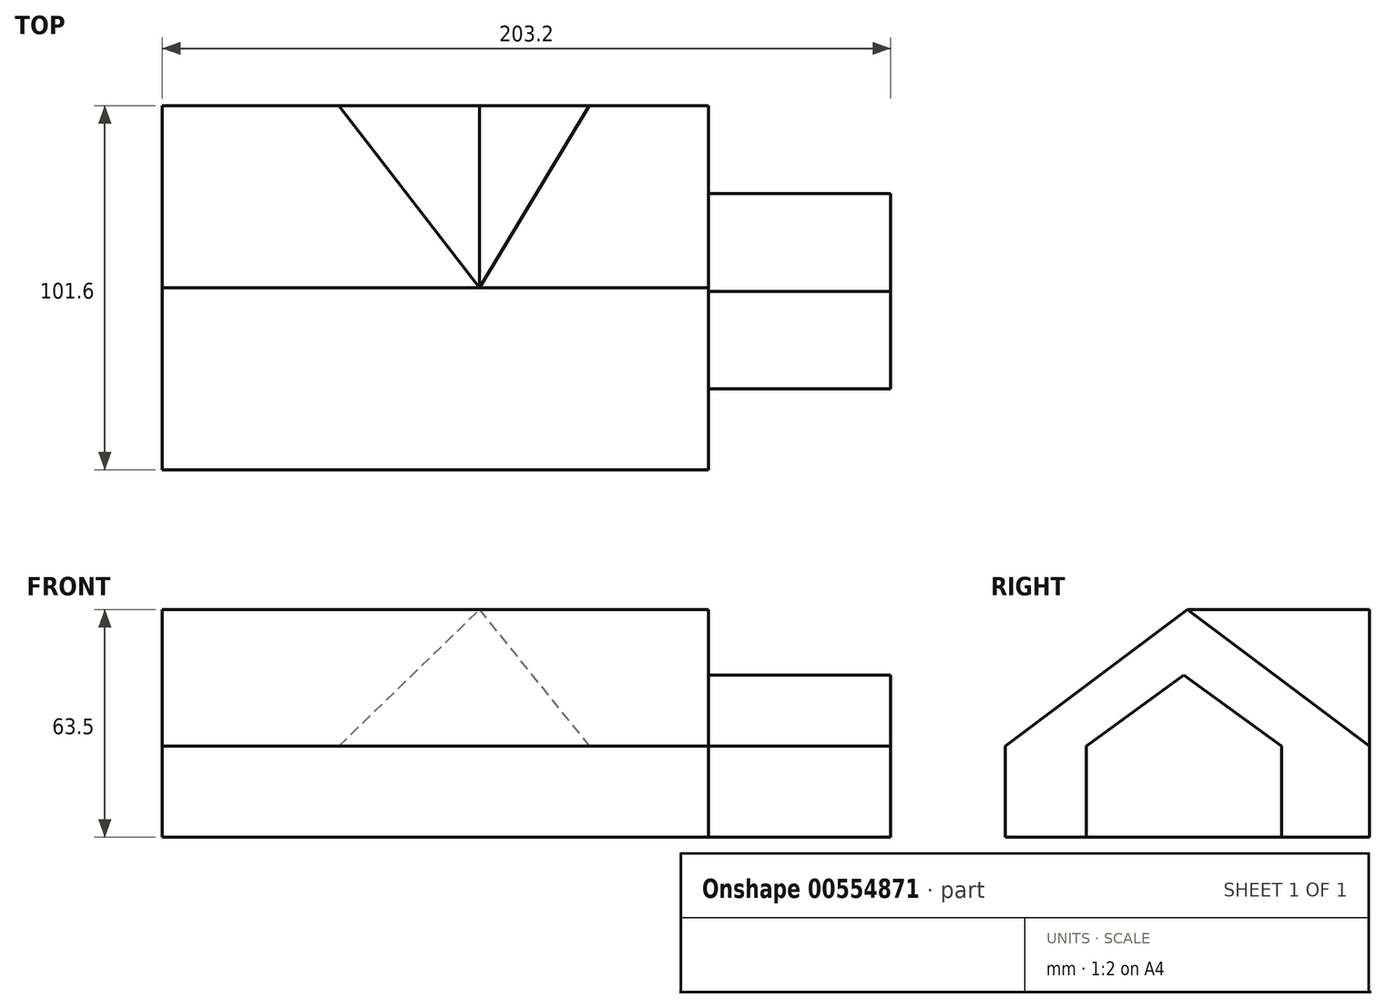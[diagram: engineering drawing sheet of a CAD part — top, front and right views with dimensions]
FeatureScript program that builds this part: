
annotation { "Feature Type Name" : "Feature", "Feature Type Description" : "" }
export const myFeature = defineFeature(function(context is Context, id is Id, definition is map)
    precondition{}
    {
        {
            var Q0;
            Q0=qCreatedBy(makeId("Right.planeOp"),FACE);
            var sketch = newSketch(context, id + "F0", { "sketchPlane" : qUnion([Q0])});
            skLineSegment(sketch, "E0.bottom", {"start": v(-40.64, 17.51) * mm, "end": v(60.96, 17.51) * mm});
            skLineSegment(sketch, "E0.top", {"start": v(-40.64, -7.89) * mm, "end": v(60.96, -7.89) * mm});
            skLineSegment(sketch, "E0.left", {"start": v(-40.64, 17.51) * mm, "end": v(-40.64, -7.89) * mm});
            skLineSegment(sketch, "E0.right", {"start": v(60.96, 17.51) * mm, "end": v(60.96, -7.89) * mm});
            skLineSegment(sketch, "E1", {"start": v(-40.64, 17.51) * mm, "end": v(10.16, 55.61) * mm});
            skPoint(sketch, "E1.endSnap0", {"position": v(10.16, 17.51) * mm});
            skLineSegment(sketch, "E2", {"start": v(10.16, 55.61) * mm, "end": v(60.96, 17.51) * mm});
            skSolve(sketch);
        }
        {
            var Q0;
            Q0=makeQuery(id+"F0.imprint","IMPRINT",FACE,{"disambiguationData":[TD([[makeQuery(id+"F0.imprint","IMPRINT",EDGE,{"derivedFrom":sQuery(id+"F0.wireOp",EDGE,"E0.bottom")}),-1.0]])]});
            var Q1;
            Q1=makeQuery(id+"F0.imprint","IMPRINT",FACE,{"disambiguationData":[TD([[makeQuery(id+"F0.imprint","IMPRINT",EDGE,{"derivedFrom":sQuery(id+"F0.wireOp",EDGE,"E0.bottom")}),1.0]])]});
            extrude(context, id + "F1", {"entities" : qUnion([Q0, Q1]), "oppositeDirection" : true, "depth" : 152.4 * mm, "offsetDistance" : 25.4 * mm});
        }
        {
            var Q0;
            Q0=makeQuery(id+"F1.opExtrude","CAP_FACE",FACE,{"disambiguationData":[OSD([sQuery(id+"F0.wireOp",EDGE,"E0.top"),sQuery(id+"F0.wireOp",EDGE,"E0.left"),sQuery(id+"F0.wireOp",EDGE,"E0.right"),sQuery(id+"F0.wireOp",EDGE,"E1"),sQuery(id+"F0.wireOp",EDGE,"E2")])],"isStart":true});
            var sketch = newSketch(context, id + "F2", { "sketchPlane" : qUnion([Q0])});
            skLineSegment(sketch, "E3.bottom", {"start": v(-18.05, 17.51) * mm, "end": v(36.4, 17.51) * mm});
            skLineSegment(sketch, "E3.top", {"start": v(-18.05, -7.89) * mm, "end": v(36.4, -7.89) * mm});
            skLineSegment(sketch, "E3.left", {"start": v(-18.05, 17.51) * mm, "end": v(-18.05, -7.89) * mm});
            skLineSegment(sketch, "E3.right", {"start": v(36.4, 17.51) * mm, "end": v(36.4, -7.89) * mm});
            skLineSegment(sketch, "E4", {"start": v(-18.05, 17.51) * mm, "end": v(9.17, 37.3) * mm});
            skPoint(sketch, "E4.endSnap0", {"position": v(9.17, 17.51) * mm});
            skLineSegment(sketch, "E5", {"start": v(9.17, 37.3) * mm, "end": v(36.4, 17.51) * mm});
            skSolve(sketch);
        }
        {
            var Q0;
            Q0=makeQuery(id+"F2.imprint","IMPRINT",FACE,{"disambiguationData":[TD([[makeQuery(id+"F2.imprint","IMPRINT",EDGE,{"derivedFrom":sQuery(id+"F2.wireOp",EDGE,"E3.bottom")}),1.0]])]});
            var Q1;
            Q1=makeQuery(id+"F2.imprint","IMPRINT",FACE,{"disambiguationData":[TD([[makeQuery(id+"F2.imprint","IMPRINT",EDGE,{"derivedFrom":sQuery(id+"F2.wireOp",EDGE,"E3.bottom")}),-1.0]])]});
            extrude(context, id + "F3", {"entities" : qUnion([Q0, Q1]), "operationType" : NewBodyOperationType.ADD, "depth" : 50.8 * mm, "offsetDistance" : 25.4 * mm});
        }
        {
            var Q0;
            Q0=makeQuery(id+"F1.opExtrude","SWEPT_FACE",FACE,{"disambiguationData":[OSD([sQuery(id+"F0.wireOp",EDGE,"E0.right")])]});
            var sketch = newSketch(context, id + "F4", { "sketchPlane" : qUnion([Q0])});
            skLineSegment(sketch, "E6", {"start": v(33.29, 17.51) * mm, "end": v(63.97, 55.61) * mm});
            skLineSegment(sketch, "E7", {"start": v(63.97, 55.61) * mm, "end": v(103.14, 17.51) * mm});
            skLineSegment(sketch, "E8", {"start": v(103.14, 17.51) * mm, "end": v(33.29, 17.51) * mm});
            skSolve(sketch);
        }
        {
            var Q0;
            Q0=makeQuery(id+"F4.imprint","IMPRINT",FACE,{"disambiguationData":[TD([[makeQuery(id+"F4.imprint","IMPRINT",EDGE,{"derivedFrom":sQuery(id+"F4.wireOp",EDGE,"E6")}),-1.0]])]});
            extrude(context, id + "F5", {"entities" : qUnion([Q0]), "operationType" : NewBodyOperationType.ADD, "oppositeDirection" : true, "depth" : 50.8 * mm, "offsetDistance" : 25.4 * mm});
        }
    });
